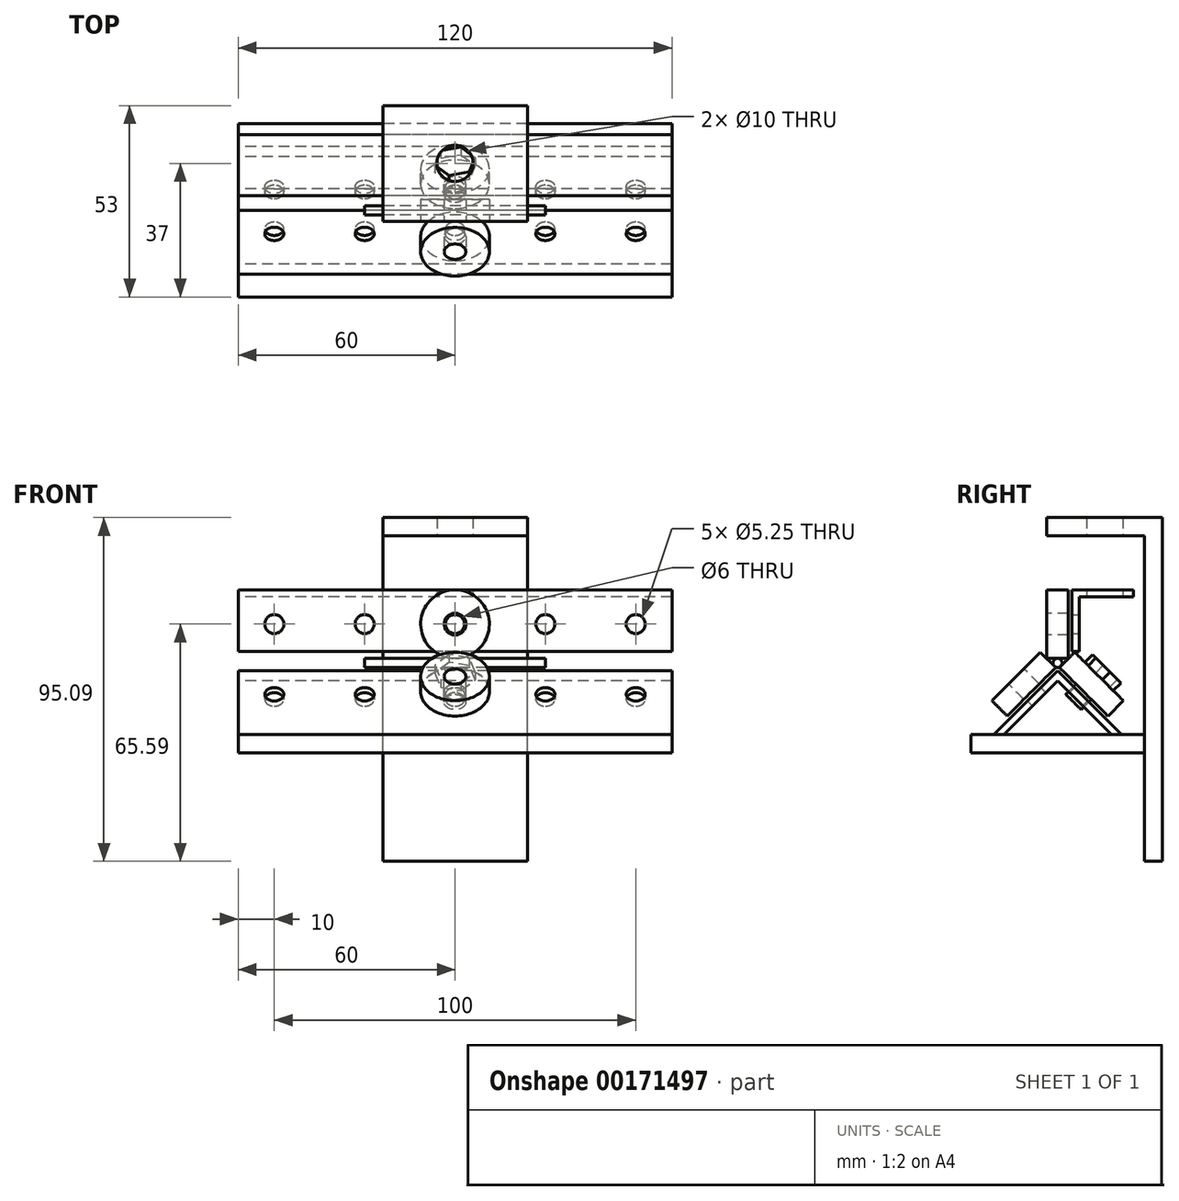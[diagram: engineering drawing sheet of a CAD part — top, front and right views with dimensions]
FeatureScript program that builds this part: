
annotation { "Feature Type Name" : "Feature", "Feature Type Description" : "" }
export const myFeature = defineFeature(function(context is Context, id is Id, definition is map)
    precondition{}
    {
        {
            var Q0;
            Q0=qCreatedBy(makeId("Right.planeOp"),FACE);
            var sketch = newSketch(context, id + "F0", { "sketchPlane" : qUnion([Q0])});
            skLineSegment(sketch, "E0", {"start": v(0, 0) * mm, "end": v(0, -20.95) * mm, "construction": true});
            skLineSegment(sketch, "E1", {"start": v(-0.5, 0) * mm, "end": v(-13.94, -13.44) * mm, "construction": true});
            skLineSegment(sketch, "E2", {"start": v(-13.94, -13.44) * mm, "end": v(-18.18, -9.2) * mm, "construction": true});
            skLineSegment(sketch, "E3", {"start": v(-18.18, -9.2) * mm, "end": v(-4.74, 4.24) * mm, "construction": true});
            skLineSegment(sketch, "E4", {"start": v(-4.74, 4.24) * mm, "end": v(-0.5, 0) * mm, "construction": true});
            skLineSegment(sketch, "E5.MirrorCS", {"start": v(4.74, 4.24) * mm, "end": v(0.5, 0) * mm, "construction": true});
            skLineSegment(sketch, "E6.MirrorCS", {"start": v(18.18, -9.2) * mm, "end": v(4.74, 4.24) * mm, "construction": true});
            skLineSegment(sketch, "E7.MirrorCS", {"start": v(13.94, -13.44) * mm, "end": v(18.18, -9.2) * mm, "construction": true});
            skLineSegment(sketch, "E8.MirrorCS", {"start": v(0.5, 0) * mm, "end": v(13.94, -13.44) * mm, "construction": true});
            skCircle(sketch, "E9", {"center": v(0, 1.62) * mm, "radius": 1.5 * mm, "construction": true});
            skCircle(sketch, "E10", {"center": v(0, 7.99) * mm, "radius": 6 * mm, "construction": true});
            skLineSegment(sketch, "E11.bottom", {"start": v(3, 2.5) * mm, "end": v(-3, 2.5) * mm, "construction": true});
            skLineSegment(sketch, "E11.top", {"start": v(3, 21.5) * mm, "end": v(-3, 21.5) * mm, "construction": true});
            skLineSegment(sketch, "E11.left", {"start": v(3, 2.5) * mm, "end": v(3, 21.5) * mm, "construction": true});
            skLineSegment(sketch, "E11.right", {"start": v(-3, 2.5) * mm, "end": v(-3, 21.5) * mm, "construction": true});
            skPoint(sketch, "E11.middle", {"position": v(0, 12) * mm});
            skCircle(sketch, "E12", {"center": v(0, 1.26) * mm, "radius": 1.24 * mm, "construction": true});
            skLineSegment(sketch, "E13", {"start": v(-8.08, 13.99) * mm, "end": v(14.73, 13.99) * mm, "construction": true});
            skLineSegment(sketch, "E14", {"start": v(-13.58, -4.6) * mm, "end": v(-9.34, -8.84) * mm, "construction": true});
            skLineSegment(sketch, "E15", {"start": v(-9.34, -0.35) * mm, "end": v(-5.1, -4.6) * mm, "construction": true});
            skLineSegment(sketch, "E16", {"start": v(5.1, -4.6) * mm, "end": v(9.34, -0.35) * mm, "construction": true});
            skLineSegment(sketch, "E17", {"start": v(9.34, -8.84) * mm, "end": v(13.58, -4.6) * mm, "construction": true});
            skLineSegment(sketch, "E18", {"start": v(-11.46, -2.47) * mm, "end": v(-7.22, -6.72) * mm, "construction": true});
            skLineSegment(sketch, "E19", {"start": v(11.46, -2.47) * mm, "end": v(7.22, -6.72) * mm, "construction": true});
            skLineSegment(sketch, "E20", {"start": v(-5.1, -4.6) * mm, "end": v(0, -9.7) * mm, "construction": true});
            skLineSegment(sketch, "E21", {"start": v(-9.34, -8.84) * mm, "end": v(-4.53, -13.65) * mm, "construction": true});
            skLineSegment(sketch, "E22", {"start": v(5.1, -4.6) * mm, "end": v(0, -9.7) * mm, "construction": true});
            skLineSegment(sketch, "E23", {"start": v(9.34, -8.84) * mm, "end": v(5.45, -12.72) * mm, "construction": true});
            skSolve(sketch);
        }
        {
            var Q0;
            Q0=qCreatedBy(makeId("Right.planeOp"),FACE);
            var sketch = newSketch(context, id + "F1", { "sketchPlane" : qUnion([Q0])});
            skLineSegment(sketch, "E24", {"start": v(-18.18, -9.2) * mm, "end": v(-13.58, -4.6) * mm});
            skLineSegment(sketch, "E25", {"start": v(-13.58, -4.6) * mm, "end": v(-9.34, -8.84) * mm});
            skLineSegment(sketch, "E26", {"start": v(-9.34, -8.84) * mm, "end": v(-13.94, -13.44) * mm});
            skLineSegment(sketch, "E27", {"start": v(-13.94, -13.44) * mm, "end": v(-18.18, -9.2) * mm});
            skLineSegment(sketch, "E28", {"start": v(0, 0) * mm, "end": v(0, -22.25) * mm, "construction": true});
            skLineSegment(sketch, "E29.bottom", {"start": v(-3, 9) * mm, "end": v(3, 9) * mm});
            skLineSegment(sketch, "E29.top", {"start": v(-3, 2.5) * mm, "end": v(3, 2.5) * mm});
            skLineSegment(sketch, "E29.left", {"start": v(-3, 9) * mm, "end": v(-3, 2.5) * mm});
            skLineSegment(sketch, "E29.right", {"start": v(3, 9) * mm, "end": v(3, 2.5) * mm});
            skLineSegment(sketch, "E30", {"start": v(-11.46, -2.47) * mm, "end": v(-7.22, -6.72) * mm, "construction": true});
            skLineSegment(sketch, "E31", {"start": v(-8.08, 12) * mm, "end": v(14.73, 12) * mm, "construction": true});
            skLineSegment(sketch, "E32.MirrorCS", {"start": v(18.18, -9.2) * mm, "end": v(13.58, -4.6) * mm});
            skLineSegment(sketch, "E33.MirrorCS", {"start": v(9.34, -8.84) * mm, "end": v(13.94, -13.44) * mm});
            skLineSegment(sketch, "E34.MirrorCS", {"start": v(13.94, -13.44) * mm, "end": v(18.18, -9.2) * mm});
            skLineSegment(sketch, "E35.MirrorCS", {"start": v(13.58, -4.6) * mm, "end": v(9.34, -8.84) * mm});
            skLineSegment(sketch, "E36.MirrorCS", {"start": v(11.46, -2.47) * mm, "end": v(7.22, -6.72) * mm, "construction": true});
            skCircle(sketch, "E37", {"center": v(0, 1.26) * mm, "radius": 1.24 * mm});
            skSolve(sketch);
        }
        {
            var Q0;
            Q0=makeQuery(id+"F1.imprint","IMPRINT",FACE,{"disambiguationData":[TD([[makeQuery(id+"F1.imprint","IMPRINT",EDGE,{"derivedFrom":sQuery(id+"F1.wireOp",EDGE,"E24")}),-1.0]])]});
            var Q1;
            Q1=sQuery(id+"F1.wireOp",EDGE,"E30");
            revolve(context, id + "F2", {"surfaceOperationType" : NewSurfaceOperationType.NEW, "entities" : qUnion([Q0]), "axis" : qUnion([Q1]), "revolveType" : RevolveType.FULL});
        }
        {
            var Q0;
            Q0=makeQuery(id+"F1.imprint","IMPRINT",FACE,{"disambiguationData":[TD([[makeQuery(id+"F1.imprint","IMPRINT",EDGE,{"derivedFrom":sQuery(id+"F1.wireOp",EDGE,"E32.MirrorCS")}),1.0]])]});
            var Q1;
            Q1=sQuery(id+"F1.wireOp",EDGE,"E36.MirrorCS");
            revolve(context, id + "F3", {"surfaceOperationType" : NewSurfaceOperationType.NEW, "entities" : qUnion([Q0]), "axis" : qUnion([Q1]), "revolveType" : RevolveType.FULL});
        }
        {
            var Q0;
            Q0=makeQuery(id+"F1.imprint","IMPRINT",FACE,{"disambiguationData":[TD([[makeQuery(id+"F1.imprint","IMPRINT",EDGE,{"derivedFrom":sQuery(id+"F1.wireOp",EDGE,"E29.bottom")}),-1.0]])]});
            var Q1;
            Q1=sQuery(id+"F1.wireOp",EDGE,"E31");
            revolve(context, id + "F4", {"surfaceOperationType" : NewSurfaceOperationType.NEW, "entities" : qUnion([Q0]), "axis" : qUnion([Q1]), "revolveType" : RevolveType.FULL});
        }
        {
            var Q0;
            Q0=makeQuery(id+"F1.imprint","IMPRINT",FACE,{"disambiguationData":[TD([[makeQuery(id+"F1.imprint","IMPRINT",EDGE,{"derivedFrom":sQuery(id+"F1.wireOp",EDGE,"E37")}),1.0]])]});
            extrude(context, id + "F5", {"entities" : qUnion([Q0]), "depth" : 25 * mm, "offsetDistance" : 25 * mm, "hasSecondDirection" : true, "secondDirectionOppositeDirection" : true, "secondDirectionDepth" : 25 * mm});
        }
        {
            var Q0;
            Q0=qCreatedBy(makeId("Right.planeOp"),FACE);
            var sketch = newSketch(context, id + "F6", { "sketchPlane" : qUnion([Q0])});
            skLineSegment(sketch, "E38", {"start": v(0, -0.91) * mm, "end": v(-17.68, -18.6) * mm});
            skLineSegment(sketch, "E39", {"start": v(-17.68, -18.6) * mm, "end": v(-14.85, -18.6) * mm});
            skLineSegment(sketch, "E40", {"start": v(-14.85, -18.6) * mm, "end": v(0, -3.74) * mm});
            skLineSegment(sketch, "E41", {"start": v(0, -3.74) * mm, "end": v(14.85, -18.6) * mm});
            skLineSegment(sketch, "E42", {"start": v(14.85, -18.6) * mm, "end": v(17.68, -18.6) * mm});
            skLineSegment(sketch, "E43", {"start": v(17.68, -18.6) * mm, "end": v(0, -0.91) * mm});
            skSolve(sketch);
        }
        {
            var Q0;
            Q0=makeQuery(id+"F6.imprint","IMPRINT",FACE,{"disambiguationData":[TD([[makeQuery(id+"F6.imprint","IMPRINT",EDGE,{"derivedFrom":sQuery(id+"F6.wireOp",EDGE,"E38")}),1.0]])]});
            extrude(context, id + "F7", {"entities" : qUnion([Q0]), "depth" : 60 * mm, "offsetDistance" : 25 * mm, "hasSecondDirection" : true, "secondDirectionOppositeDirection" : true, "secondDirectionDepth" : 60 * mm});
        }
        {
            var Q0;
            Q0=makeQuery(id+"F7.opExtrude","SWEPT_FACE",FACE,{"disambiguationData":[OSD([sQuery(id+"F6.wireOp",EDGE,"E38")])]});
            var sketch = newSketch(context, id + "F8", { "sketchPlane" : qUnion([Q0])});
            skLineSegment(sketch, "E44", {"start": v(-50, -9.85) * mm, "end": v(-25, -9.85) * mm, "construction": true});
            skLineSegment(sketch, "E45", {"start": v(-25, -9.85) * mm, "end": v(0, -9.85) * mm, "construction": true});
            skLineSegment(sketch, "E46", {"start": v(0, -9.85) * mm, "end": v(25, -9.85) * mm, "construction": true});
            skLineSegment(sketch, "E47", {"start": v(25, -9.85) * mm, "end": v(50, -9.85) * mm, "construction": true});
            skSolve(sketch);
        }
        {
            var Q0;
            Q0=makeQuery(id+"F7.opExtrude","SWEPT_FACE",FACE,{"disambiguationData":[OSD([sQuery(id+"F6.wireOp",EDGE,"E43")])]});
            var sketch = newSketch(context, id + "F9", { "sketchPlane" : qUnion([Q0])});
            skLineSegment(sketch, "E48", {"start": v(-50, -9.85) * mm, "end": v(-25, -9.85) * mm, "construction": true});
            skLineSegment(sketch, "E49", {"start": v(-25, -9.85) * mm, "end": v(0, -9.85) * mm, "construction": true});
            skLineSegment(sketch, "E50", {"start": v(0, -9.85) * mm, "end": v(25, -9.85) * mm, "construction": true});
            skLineSegment(sketch, "E51", {"start": v(25, -9.85) * mm, "end": v(50, -9.85) * mm, "construction": true});
            skSolve(sketch);
        }
        {
            var Q0;
            Q0=qCreatedBy(makeId("Right.planeOp"),FACE);
            var sketch = newSketch(context, id + "F10", { "sketchPlane" : qUnion([Q0])});
            skLineSegment(sketch, "E52.bottom", {"start": v(-24, -18.6) * mm, "end": v(24, -18.6) * mm});
            skLineSegment(sketch, "E52.top", {"start": v(-24, -23.6) * mm, "end": v(24, -23.6) * mm});
            skLineSegment(sketch, "E52.left", {"start": v(-24, -18.6) * mm, "end": v(-24, -23.6) * mm});
            skLineSegment(sketch, "E52.right", {"start": v(24, -18.6) * mm, "end": v(24, -23.6) * mm});
            skLineSegment(sketch, "E53.bottom", {"start": v(24, -23.6) * mm, "end": v(29, -23.6) * mm});
            skLineSegment(sketch, "E53.top", {"start": v(24, 41.5) * mm, "end": v(29, 41.5) * mm});
            skLineSegment(sketch, "E53.left", {"start": v(24, -23.6) * mm, "end": v(24, 41.5) * mm});
            skLineSegment(sketch, "E53.right", {"start": v(29, -23.6) * mm, "end": v(29, 41.5) * mm});
            skLineSegment(sketch, "E54.bottom", {"start": v(24, 41.5) * mm, "end": v(-3, 41.5) * mm});
            skLineSegment(sketch, "E54.top", {"start": v(24, 36.5) * mm, "end": v(-3, 36.5) * mm});
            skLineSegment(sketch, "E54.left", {"start": v(24, 41.5) * mm, "end": v(24, 36.5) * mm});
            skLineSegment(sketch, "E54.right", {"start": v(-3, 41.5) * mm, "end": v(-3, 36.5) * mm});
            skLineSegment(sketch, "E55.bottom", {"start": v(4, 4.5) * mm, "end": v(6, 4.5) * mm});
            skLineSegment(sketch, "E55.top", {"start": v(4, 21.5) * mm, "end": v(6, 21.5) * mm});
            skLineSegment(sketch, "E55.left", {"start": v(4, 4.5) * mm, "end": v(4, 21.5) * mm});
            skLineSegment(sketch, "E55.right", {"start": v(6, 4.5) * mm, "end": v(6, 19.5) * mm});
            skLineSegment(sketch, "E56.bottom", {"start": v(6, 21.5) * mm, "end": v(21, 21.5) * mm});
            skLineSegment(sketch, "E56.top", {"start": v(6, 19.5) * mm, "end": v(21, 19.5) * mm});
            skLineSegment(sketch, "E56.right", {"start": v(21, 21.5) * mm, "end": v(21, 19.5) * mm});
            skLineSegment(sketch, "E57", {"start": v(-11.95, 2.5) * mm, "end": v(-8.8, 2.5) * mm, "construction": true});
            skLineSegment(sketch, "E58", {"start": v(-11.88, 13.99) * mm, "end": v(-9.14, 13.99) * mm, "construction": true});
            skLineSegment(sketch, "E59.top", {"start": v(24, -53.6) * mm, "end": v(29, -53.6) * mm});
            skLineSegment(sketch, "E59.left", {"start": v(24, -23.6) * mm, "end": v(24, -53.6) * mm});
            skLineSegment(sketch, "E59.right", {"start": v(29, -23.6) * mm, "end": v(29, -53.6) * mm});
            skSolve(sketch);
        }
        {
            var Q0;
            {var subQ0=sQuery(id+"F10.wireOp",EDGE,"E52.bottom");Q0=makeQuery(id+"F10.imprint","IMPRINT",FACE,{"disambiguationData":[TD([[makeQuery(id+"F10.imprint","IMPRINT",EDGE,{"derivedFrom":subQ0}),-1.0]])]});}
            extrude(context, id + "F11", {"entities" : qUnion([Q0]), "depth" : 60 * mm, "offsetDistance" : 25 * mm, "hasSecondDirection" : true, "secondDirectionOppositeDirection" : true, "secondDirectionDepth" : 60 * mm});
        }
        {
            var Q0;
            Q0=makeQuery(id+"F10.imprint","IMPRINT",FACE,{"disambiguationData":[TD([[makeQuery(id+"F10.imprint","IMPRINT",EDGE,{"derivedFrom":sQuery(id+"F10.wireOp",EDGE,"E55.bottom")}),1.0]])]});
            extrude(context, id + "F12", {"entities" : qUnion([Q0]), "depth" : 60 * mm, "offsetDistance" : 25 * mm, "hasSecondDirection" : true, "secondDirectionOppositeDirection" : true, "secondDirectionDepth" : 60 * mm});
        }
        {
            var Q0;
            Q0=makeQuery(id+"F10.imprint","IMPRINT",FACE,{"disambiguationData":[TD([[makeQuery(id+"F10.imprint","IMPRINT",EDGE,{"derivedFrom":sQuery(id+"F10.wireOp",EDGE,"E54.bottom")}),1.0]])]});
            var Q1;
            Q1=makeQuery(id+"F10.imprint","IMPRINT",FACE,{"disambiguationData":[TD([[makeQuery(id+"F10.imprint","IMPRINT",EDGE,{"derivedFrom":sQuery(id+"F10.wireOp",EDGE,"E53.top")}),-1.0]])]});
            var Q2;
            Q2=makeQuery(id+"F10.imprint","IMPRINT",FACE,{"disambiguationData":[TD([[makeQuery(id+"F10.imprint","IMPRINT",EDGE,{"derivedFrom":sQuery(id+"F10.wireOp",EDGE,"E53.bottom")}),-1.0]])]});
            extrude(context, id + "F13", {"entities" : qUnion([Q0, Q1, Q2]), "operationType" : NewBodyOperationType.ADD, "depth" : 20 * mm, "offsetDistance" : 25 * mm, "hasSecondDirection" : true, "secondDirectionOppositeDirection" : true, "secondDirectionDepth" : 20 * mm});
        }
        {
            var Q0;
            Q0=makeQuery(id+"F12.opExtrude","SWEPT_FACE",FACE,{"disambiguationData":[OSD([sQuery(id+"F10.wireOp",EDGE,"E55.left")])]});
            var sketch = newSketch(context, id + "F14", { "sketchPlane" : qUnion([Q0])});
            skLineSegment(sketch, "E60", {"start": v(-50, 12) * mm, "end": v(-25, 12) * mm, "construction": true});
            skLineSegment(sketch, "E61", {"start": v(-25, 12) * mm, "end": v(0, 12) * mm, "construction": true});
            skLineSegment(sketch, "E62", {"start": v(0, 12) * mm, "end": v(25, 12) * mm, "construction": true});
            skLineSegment(sketch, "E63", {"start": v(25, 12) * mm, "end": v(50, 12) * mm, "construction": true});
            skSolve(sketch);
        }
        {
            var Q0;
            Q0=sQuery(id+"F9.wireOp",VERTEX,"E48.start");
            var Q1;
            Q1=sQuery(id+"F9.wireOp",VERTEX,"E48.end");
            var Q2;
            Q2=sQuery(id+"F9.wireOp",VERTEX,"E49.end");
            var Q3;
            Q3=sQuery(id+"F9.wireOp",VERTEX,"E50.end");
            var Q4;
            Q4=sQuery(id+"F9.wireOp",VERTEX,"E51.end");
            var Q5;
            Q5=sQuery(id+"F8.wireOp",VERTEX,"E44.start");
            var Q6;
            Q6=sQuery(id+"F8.wireOp",VERTEX,"E44.end");
            var Q7;
            Q7=sQuery(id+"F8.wireOp",VERTEX,"E45.end");
            var Q8;
            Q8=sQuery(id+"F8.wireOp",VERTEX,"E46.end");
            var Q9;
            Q9=sQuery(id+"F8.wireOp",VERTEX,"E47.end");
            var Q10;
            Q10=sQuery(id+"F14.wireOp",VERTEX,"E60.start");
            var Q11;
            Q11=sQuery(id+"F14.wireOp",VERTEX,"E60.end");
            var Q12;
            Q12=sQuery(id+"F14.wireOp",VERTEX,"E61.end");
            var Q13;
            Q13=sQuery(id+"F14.wireOp",VERTEX,"E62.end");
            var Q14;
            Q14=sQuery(id+"F14.wireOp",VERTEX,"E63.end");
            var Q15;
            Q15=makeQuery(id+"F7.opExtrude","SWEPT_BODY",BODY,{"disambiguationData":[OSD([sQuery(id+"F6.wireOp",EDGE,"E38"),sQuery(id+"F6.wireOp",EDGE,"E39"),sQuery(id+"F6.wireOp",EDGE,"E40"),sQuery(id+"F6.wireOp",EDGE,"E41"),sQuery(id+"F6.wireOp",EDGE,"E42"),sQuery(id+"F6.wireOp",EDGE,"E43")])]});
            var Q16;
            Q16=makeQuery(id+"F12.opExtrude","SWEPT_BODY",BODY,{"disambiguationData":[OSD([sQuery(id+"F10.wireOp",EDGE,"E55.bottom"),sQuery(id+"F10.wireOp",EDGE,"E55.top"),sQuery(id+"F10.wireOp",EDGE,"E55.left"),sQuery(id+"F10.wireOp",EDGE,"E55.right"),sQuery(id+"F10.wireOp",EDGE,"E56.bottom"),sQuery(id+"F10.wireOp",EDGE,"E56.top"),sQuery(id+"F10.wireOp",EDGE,"E56.right")])]});
            hole(context, id + "F15", {"style" : HoleStyle.SIMPLE, "endStyle" : HoleEndStyle.BLIND, "standardTappedOrClearance" : lookupTablePath({ "standard" : "ISO", "engagement" : "75%", "pitch" : "0.75 mm", "size" : "M6", "type" : "Tapped" }), "standardBlindInLast" : lookupTablePath({ "standard" : "ISO", "fit" : "Normal", "engagement" : "75%", "pitch" : "0.75 mm", "size" : "M6", "type" : "Clearance & tapped" }), "holeDiameter" : 5.25 * mm, "majorDiameter" : 6 * mm, "showTappedDepth" : true, "holeDepth" : 8.15 * mm, "tappedDepth" : 5.9 * mm, "tapClearance" : 3, "locations" : qUnion([Q0, Q1, Q2, Q3, Q4, Q5, Q6, Q7, Q8, Q9, Q10, Q11, Q12, Q13, Q14]), "scope" : qUnion([Q15, Q16]), "startStyle" : HoleStartStyle.SKETCH});
        }
        {
            var Q0;
            Q0=makeQuery(id+"F13.opExtrude","SWEPT_FACE",FACE,{"disambiguationData":[OSD([sQuery(id+"F10.wireOp",EDGE,"E53.top"),sQuery(id+"F10.wireOp",EDGE,"E54.bottom")])]});
            var sketch = newSketch(context, id + "F16", { "sketchPlane" : qUnion([Q0])});
            skLineSegment(sketch, "E64", {"start": v(20, 13) * mm, "end": v(0, 13) * mm, "construction": true});
            skLineSegment(sketch, "E65", {"start": v(0, 13) * mm, "end": v(0, -3) * mm, "construction": true});
            skPoint(sketch, "E66", {"position": v(-15.43, 4.9) * mm});
            skSolve(sketch);
        }
        {
            var Q0;
            Q0=sQuery(id+"F16.wireOp",VERTEX,"E64.end");
            var Q1;
            Q1=makeQuery(id+"F11.opExtrude","SWEPT_BODY",BODY,{"disambiguationData":[OSD([sQuery(id+"F10.wireOp",EDGE,"E52.bottom"),sQuery(id+"F10.wireOp",EDGE,"E52.top"),sQuery(id+"F10.wireOp",EDGE,"E52.left"),sQuery(id+"F10.wireOp",EDGE,"E53.left")])]});
            var Q2;
            Q2=makeQuery(id+"F12.opExtrude","SWEPT_BODY",BODY,{"disambiguationData":[OSD([sQuery(id+"F10.wireOp",EDGE,"E55.bottom"),sQuery(id+"F10.wireOp",EDGE,"E55.top"),sQuery(id+"F10.wireOp",EDGE,"E55.left"),sQuery(id+"F10.wireOp",EDGE,"E55.right"),sQuery(id+"F10.wireOp",EDGE,"E56.bottom"),sQuery(id+"F10.wireOp",EDGE,"E56.top"),sQuery(id+"F10.wireOp",EDGE,"E56.right")])]});
            hole(context, id + "F17", {"style" : HoleStyle.SIMPLE, "endStyle" : HoleEndStyle.BLIND, "holeDiameter" : 10 * mm, "majorDiameter" : 10 * mm, "holeDepth" : 54.5 * mm, "tappedDepth" : 50 * mm, "tapClearance" : 3, "locations" : qUnion([Q0]), "scope" : qUnion([Q1, Q2]), "startStyle" : HoleStartStyle.SKETCH});
        }
        {
            var Q0;
            Q0=qCreatedBy(makeId("Right.planeOp"),FACE);
            var sketch = newSketch(context, id + "F18", { "sketchPlane" : qUnion([Q0])});
            skLineSegment(sketch, "E67", {"start": v(13.47, -0.46) * mm, "end": v(3.45, -10.49) * mm, "construction": true});
            skLineSegment(sketch, "E68", {"start": v(4.39, -9.55) * mm, "end": v(11.46, -2.47) * mm});
            skLineSegment(sketch, "E69", {"start": v(11.46, -2.47) * mm, "end": v(13.58, -4.6) * mm});
            skLineSegment(sketch, "E70", {"start": v(13.58, -4.6) * mm, "end": v(6.51, -11.67) * mm});
            skLineSegment(sketch, "E71", {"start": v(6.51, -11.67) * mm, "end": v(4.39, -9.55) * mm});
            skSolve(sketch);
        }
        {
            var Q0;
            Q0=makeQuery(id+"F18.imprint","IMPRINT",FACE,{"disambiguationData":[TD([[makeQuery(id+"F18.imprint","IMPRINT",EDGE,{"derivedFrom":sQuery(id+"F18.wireOp",EDGE,"E68")}),-1.0]])]});
            var Q1;
            Q1=sQuery(id+"F18.wireOp",EDGE,"E67");
            revolve(context, id + "F19", {"surfaceOperationType" : NewSurfaceOperationType.NEW, "entities" : qUnion([Q0]), "axis" : qUnion([Q1]), "revolveType" : RevolveType.FULL});
        }
        {
            var Q0;
            Q0=makeQuery(id+"F19.opRevolve","SWEPT_FACE",FACE,{"disambiguationData":[OSD([sQuery(id+"F18.wireOp",EDGE,"E69")])]});
            var sketch = newSketch(context, id + "F20", { "sketchPlane" : qUnion([Q0])});
            skCircle(sketch, "E72.cCircle", {"center": v(0, -9.85) * mm, "radius": 5 * mm, "construction": true});
            skLineSegment(sketch, "E72.0", {"start": v(5.61, -8.5) * mm, "end": v(3.97, -14.04) * mm});
            skLineSegment(sketch, "E72.1", {"start": v(3.97, -14.04) * mm, "end": v(-1.64, -15.39) * mm});
            skLineSegment(sketch, "E72.2", {"start": v(-1.64, -15.39) * mm, "end": v(-5.61, -11.2) * mm});
            skLineSegment(sketch, "E72.3", {"start": v(-5.61, -11.2) * mm, "end": v(-3.97, -5.66) * mm});
            skLineSegment(sketch, "E72.4", {"start": v(-3.97, -5.66) * mm, "end": v(1.64, -4.32) * mm});
            skLineSegment(sketch, "E72.5", {"start": v(1.64, -4.32) * mm, "end": v(5.61, -8.5) * mm});
            skPoint(sketch, "E72.0.midPoint", {"position": v(4.8, -11.28) * mm});
            skSolve(sketch);
        }
        {
            var Q0;
            Q0=makeQuery(id+"F20.imprint","IMPRINT",FACE,{"disambiguationData":[TD([[makeQuery(id+"F20.imprint","IMPRINT",EDGE,{"derivedFrom":sQuery(id+"F20.wireOp",EDGE,"E72.0")}),-1.0]])]});
            var Q1;
            Q1=makeQuery(id+"F20.imprint","IMPRINT",FACE,{"disambiguationData":[TD([[makeQuery(id+"F20.imprint","IMPRINT",EDGE,{"derivedFrom":makeQuery(id+"F19.opRevolve","SWEPT_EDGE",EDGE,{"disambiguationData":[OSD([sQuery(id+"F18.wireOp",EDGE,"E69"),sQuery(id+"F18.wireOp",EDGE,"E70")])]})}),1.0]])]});
            extrude(context, id + "F21", {"entities" : qUnion([Q0, Q1]), "operationType" : NewBodyOperationType.ADD, "depth" : 3 * mm, "offsetDistance" : 25 * mm});
        }
    });
